# Revit family: 54802107(2022)
name_source: partatom
category: Plumbing Fixtures
units: mm (PartAtom-declared; Revit-internal decimal feet)

## family parameters
Always vertical = Yes
Cut with Voids When Loaded = No
OmniClass Number = 23.45.55.00
OmniClass Title = Sanitary Faucets, Wastes
Part Type = Normal
Room Calculation Point = No
Round Connector Dimension = Use Diameter
Shared = No
Work Plane-Based = No

## types (3) — shared parameters
3D View = https://static.hansa.com
Advanced Features = Inner body made of DZR brass
Aerator = PCA® - constant flow rate regardless of pressure variations
AssetType = Fixed
Backflow Prevention EN1717 = AA
BodyMaterial = Brass
Brand = HANSA
Catalog Drawing URL = http://static.hansa.com
Concealed Parts = Rosette plate frame;Square rosette
Connection Size = G1/2
Dimension Drawing URL = http://static.hansa.com
DurationUnit = Year
EN Standard = EN 817
FDV Document URL = http://www.hansa.com
Features = Trim Kit;Single-lever
Finish = Polished
Flow Drawing URL = http://static.hansa.com
Flow Rate At 300kPa = 0.0 L/s
Flow Rate At 300kPa With Flow Controller = 0.0 L/s
Flow Rate At 300kPa With Flow Reducers = 0.0 L/s
Group = Washbasin faucet
IfcExportAs = IfcValveType
IfcExportType = FAUCET
Installation Type = Concealed wall mounting
Installation and Maintenance Guide URL = http://static.hansa.com
Interactive AR View URL = https://static.hansa.com
Lever Handle = Single operating lever/handle;Pin shape;Hot/Cold symbols
Manufacturer = HANSA
ManufacturerName = HANSA
ManufacturerURL = http://www.hansa.com
Material = Brass
Max. Hot Water Supply = 80 °C
Mobile Product Information URL = http://mpi.hansa.com
NBSDescription = Water supply fittings for wash basins and troughs
NBSReference = 45-35-70/371
NominalDepth = 190 mm  [stored 0.62336 ft]
NominalHeight = 126 mm
NominalWidth = 175 mm
Product Family = HANSAVANTIS Style
Product Image URL = http://static.hansa.com
Product URL = http://static.hansa.com
Sales Package dimensions (LxWxH) = 210 x 165 x 60
Shape = Sculptured
Size = 175x190x125 mm
Spout Projection = 179 mm
Spout Type = Fixed spout
Technical DataSheet URL = http://www.hansa.com
Temperature Adjustments = Limitation option for maximum temperature and flow-rate ;Adjustable hot water stop (included, retrofittable)
URL Declaration Of Performance (DOP) = http://static.hansa.com
URL Declaration of Asbestos = http://static.hansa.com
URL Declaration of Conformity = http://static.hansa.com
URL Declaration of SCIP = http://static.hansa.com
URL EU Packaging Declaration = http://static.hansa.com
URL EcoLabel Declaration = http://static.hansa.com
URL Materials Declaration = http://www.hansa.com
URL REACH = http://static.hansa.com
URL UWL = http://static.hansa.com
Uniclass2 = Pr_40_30_96_96
Uniclass2015Description = Washbasin manual water supply sets
Uniclass2015Reference = Pr_40_20_87_96
Version = 1
VersionDate = 20/02/2024
Warranty Information URL = http://warranty.hansa.com
WarrantyDescription = http://warranty.hansa.com
WarrantyDurationUnit = Year
zero-valued in all types: CloseOffRating, Default Elevation, FlowCoefficient

## per-type parameters (varying)
- 54802107 Cover part for washbasin faucet - Chrome: 2D/3D/BIM Files URL=http://static.hansa.com; BIMObjectName=54802107(2023); CO2 Emissions (A1-A3)=13.7; CO2 Emissions (A4)=0.23; CO2 Emissions (B7)=1158; CO2 Emissions (C2)=0.01; CO2 Emissions (C3)=0.01; CO2 Emissions (C4)=0.18; CO2 Emissions (D)=-4.24; Color=Chrome; EAN Number=4057304017278; ETIM Class Number=EC010546 Mechanical control system for shower; FaucetMainMaterial=Chrome; Market=International;Germany;Austria;Belgium;Netherlands;France;Czech Republic;Slovakia;Italy;Spain; Model=54802107 Cover part for washbasin faucet; ModelReference=54802107; Name=54802107 Cover part for washbasin faucet; Name_en=54802107 Cover part for washbasin faucet; Product Code=54802107; Spare-Part Information URL=http://static.hansa.com; Surface treatment=Chrome; Type=0; UNSPSC Class Number=30181700 Faucets or taps; URL Environmental Product Declaration EPD=http://www.hansa.com Group EPD_Cover part for bath and shower faucet.pdf; Working Pressure=50 - 1000 kPa
- 5480210780 Cover part for washbasin faucet - Brushed Steel: BIMObjectName=5480210780(2023); CO2 Emissions (A1-A3)=0; CO2 Emissions (A4)=0; CO2 Emissions (B7)=0; CO2 Emissions (C2)=0; CO2 Emissions (C3)=0; CO2 Emissions (C4)=0; CO2 Emissions (D)=0; Color=Brushed steel; EAN Number=4057304020452; FaucetMainMaterial=Brushed Steel; Model=5480210780 Cover part for washbasin faucet; ModelReference=5480210780; Name=5480210780 Cover part for washbasin faucet; Name_en=5480210780 Cover part for washbasin faucet; Product Code=5480210780; Surface treatment=Brushed steel; Type=80; Working Pressure=50-1000 kPa
- 5480210781 Cover part for washbasin faucet - Brushed Bronze: BIMObjectName=5480210781(2023); CO2 Emissions (A1-A3)=0; CO2 Emissions (A4)=0; CO2 Emissions (B7)=0; CO2 Emissions (C2)=0; CO2 Emissions (C3)=0; CO2 Emissions (C4)=0; CO2 Emissions (D)=0; Color=BrushedBronze; EAN Number=4057304020469; FaucetMainMaterial=Brushed Bronze; Model=5480210781 Cover part for washbasin faucet; ModelReference=5480210781; Name=5480210781 Cover part for washbasin faucet; Name_en=5480210781 Cover part for washbasin faucet; Product Code=5480210781; Surface treatment=BrushedBronze; Type=81; Working Pressure=50-1000 kPa

note: [stored X ft] marks values corroborated as IEEE doubles in the binary element streams (Revit-internal decimal feet)

## geometry (parser evidence)
native form markers: Sweep x6
no freeform markers — native parametric forms only
